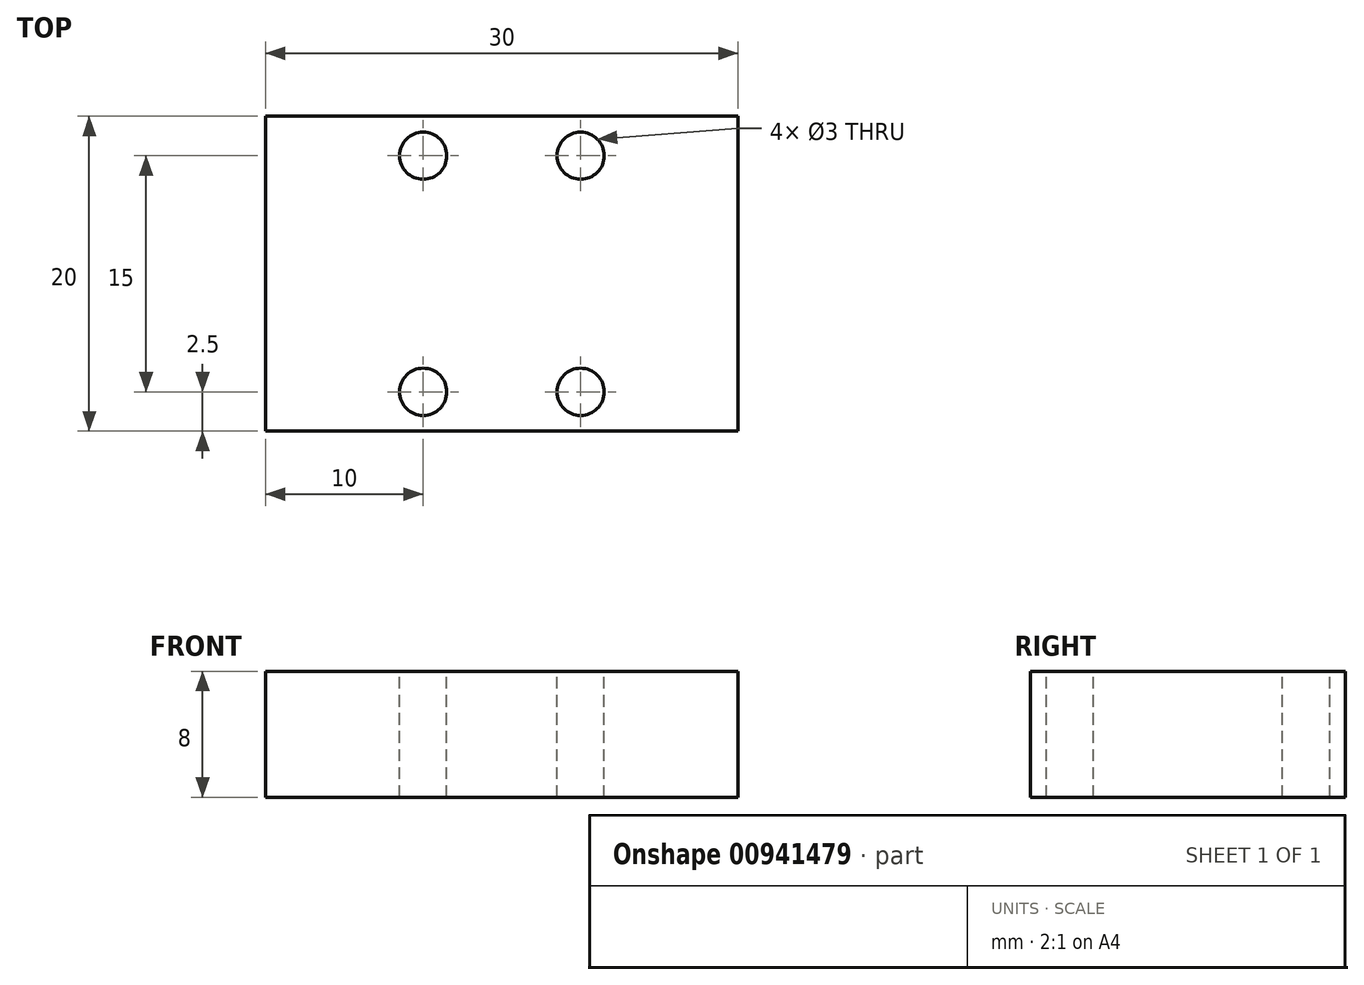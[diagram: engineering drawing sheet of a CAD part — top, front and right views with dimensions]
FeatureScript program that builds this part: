
annotation { "Feature Type Name" : "Feature", "Feature Type Description" : "" }
export const myFeature = defineFeature(function(context is Context, id is Id, definition is map)
    precondition{}
    {
        {
            var Q0;
            Q0=qCreatedBy(makeId("Top.planeOp"),FACE);
            var sketch = newSketch(context, id + "F0", { "sketchPlane" : qUnion([Q0])});
            skLineSegment(sketch, "E0.bottom", {"start": v(15, -10) * mm, "end": v(-15, -10) * mm});
            skLineSegment(sketch, "E0.top", {"start": v(15, 10) * mm, "end": v(-15, 10) * mm});
            skLineSegment(sketch, "E0.left", {"start": v(15, -10) * mm, "end": v(15, 10) * mm});
            skLineSegment(sketch, "E0.right", {"start": v(-15, -10) * mm, "end": v(-15, 10) * mm});
            skPoint(sketch, "E0.middle", {"position": v(0, 0) * mm});
            skSolve(sketch);
        }
        {
            var Q0;
            Q0=makeQuery(id+"F0.imprint","IMPRINT",FACE,{"disambiguationData":[TD([[makeQuery(id+"F0.imprint","IMPRINT",EDGE,{"derivedFrom":sQuery(id+"F0.wireOp",EDGE,"E0.bottom")}),-1.0]])]});
            extrude(context, id + "F1", {"entities" : qUnion([Q0]), "flatOperationType" : FlatOperationType.REMOVE, "depth" : 8 * mm, "offsetDistance" : 25 * mm, "domain" : OperationDomain.MODEL});
        }
        {
            var Q0;
            Q0=makeQuery(id+"F1.opExtrude","CAP_FACE",FACE,{"disambiguationData":[OSD([sQuery(id+"F0.wireOp",EDGE,"E0.bottom"),sQuery(id+"F0.wireOp",EDGE,"E0.top"),sQuery(id+"F0.wireOp",EDGE,"E0.left"),sQuery(id+"F0.wireOp",EDGE,"E0.right")])],"isStart":false});
            var sketch = newSketch(context, id + "F2", { "sketchPlane" : qUnion([Q0])});
            skCircle(sketch, "E1", {"center": v(-5, 7.5) * mm, "radius": 1.5 * mm});
            skCircle(sketch, "E2", {"center": v(5, 7.5) * mm, "radius": 1.5 * mm});
            skCircle(sketch, "E3", {"center": v(-5, -7.5) * mm, "radius": 1.5 * mm});
            skCircle(sketch, "E4", {"center": v(5, -7.5) * mm, "radius": 1.5 * mm});
            skSolve(sketch);
        }
        {
            var Q0;
            Q0=makeQuery(id+"F2.imprint","IMPRINT",FACE,{"disambiguationData":[TD([[makeQuery(id+"F2.imprint","IMPRINT",EDGE,{"derivedFrom":sQuery(id+"F2.wireOp",EDGE,"E1")}),1.0]])]});
            var Q1;
            Q1=makeQuery(id+"F2.imprint","IMPRINT",FACE,{"disambiguationData":[TD([[makeQuery(id+"F2.imprint","IMPRINT",EDGE,{"derivedFrom":sQuery(id+"F2.wireOp",EDGE,"E2")}),1.0]])]});
            var Q2;
            Q2=makeQuery(id+"F2.imprint","IMPRINT",FACE,{"disambiguationData":[TD([[makeQuery(id+"F2.imprint","IMPRINT",EDGE,{"derivedFrom":sQuery(id+"F2.wireOp",EDGE,"E4")}),1.0]])]});
            var Q3;
            Q3=makeQuery(id+"F2.imprint","IMPRINT",FACE,{"disambiguationData":[TD([[makeQuery(id+"F2.imprint","IMPRINT",EDGE,{"derivedFrom":sQuery(id+"F2.wireOp",EDGE,"E3")}),1.0]])]});
            extrude(context, id + "F3", {"entities" : qUnion([Q0, Q1, Q2, Q3]), "operationType" : NewBodyOperationType.REMOVE, "endBound" : BoundingType.THROUGH_ALL, "oppositeDirection" : true, "depth" : 4 * mm, "offsetDistance" : 25 * mm});
        }
    });
